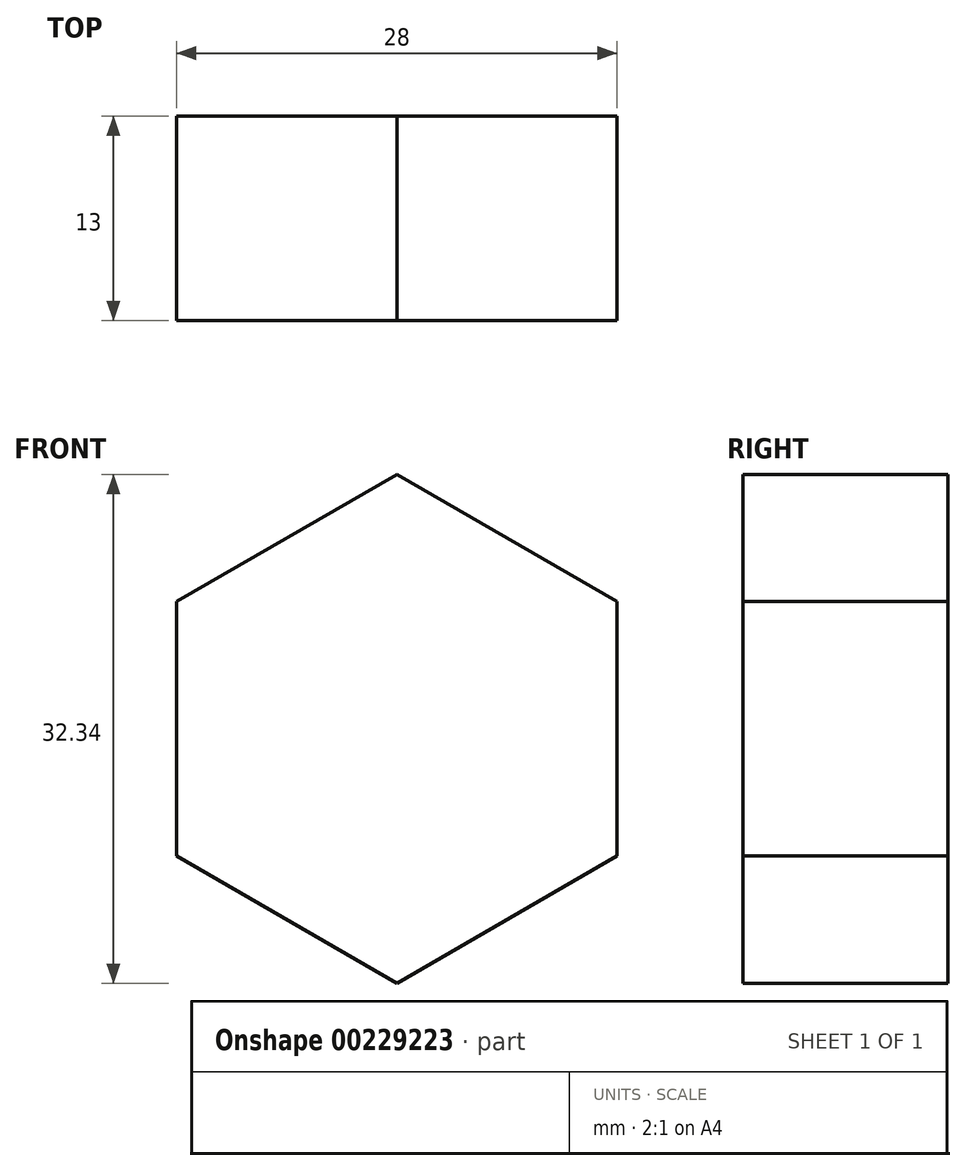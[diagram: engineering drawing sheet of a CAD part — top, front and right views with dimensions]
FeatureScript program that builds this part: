
annotation { "Feature Type Name" : "Feature", "Feature Type Description" : "" }
export const myFeature = defineFeature(function(context is Context, id is Id, definition is map)
    precondition{}
    {
        {
            var Q0;
            Q0=qCreatedBy(makeId("Front.planeOp"),FACE);
            var sketch = newSketch(context, id + "F0", { "sketchPlane" : qUnion([Q0])});
            skCircle(sketch, "E0.cCircle", {"center": v(0, 0) * mm, "radius": 14 * mm, "construction": true});
            skLineSegment(sketch, "E0.0", {"start": v(-14, 8.08) * mm, "end": v(0, 16.17) * mm});
            skLineSegment(sketch, "E0.1", {"start": v(0, 16.17) * mm, "end": v(14, 8.08) * mm});
            skLineSegment(sketch, "E0.2", {"start": v(14, 8.08) * mm, "end": v(14, -8.08) * mm});
            skLineSegment(sketch, "E0.3", {"start": v(14, -8.08) * mm, "end": v(0, -16.17) * mm});
            skLineSegment(sketch, "E0.4", {"start": v(0, -16.17) * mm, "end": v(-14, -8.08) * mm});
            skLineSegment(sketch, "E0.5", {"start": v(-14, -8.08) * mm, "end": v(-14, 8.08) * mm});
            skPoint(sketch, "E0.0.midPoint", {"position": v(-7, 12.12) * mm});
            skSolve(sketch);
        }
        {
            var Q0;
            Q0=makeQuery(id+"F0.imprint","IMPRINT",FACE,{"disambiguationData":[TD([[makeQuery(id+"F0.imprint","IMPRINT",EDGE,{"derivedFrom":sQuery(id+"F0.wireOp",EDGE,"E0.0")}),-1.0]])]});
            extrude(context, id + "F1", {"entities" : qUnion([Q0]), "depth" : 13 * mm});
        }
    });
